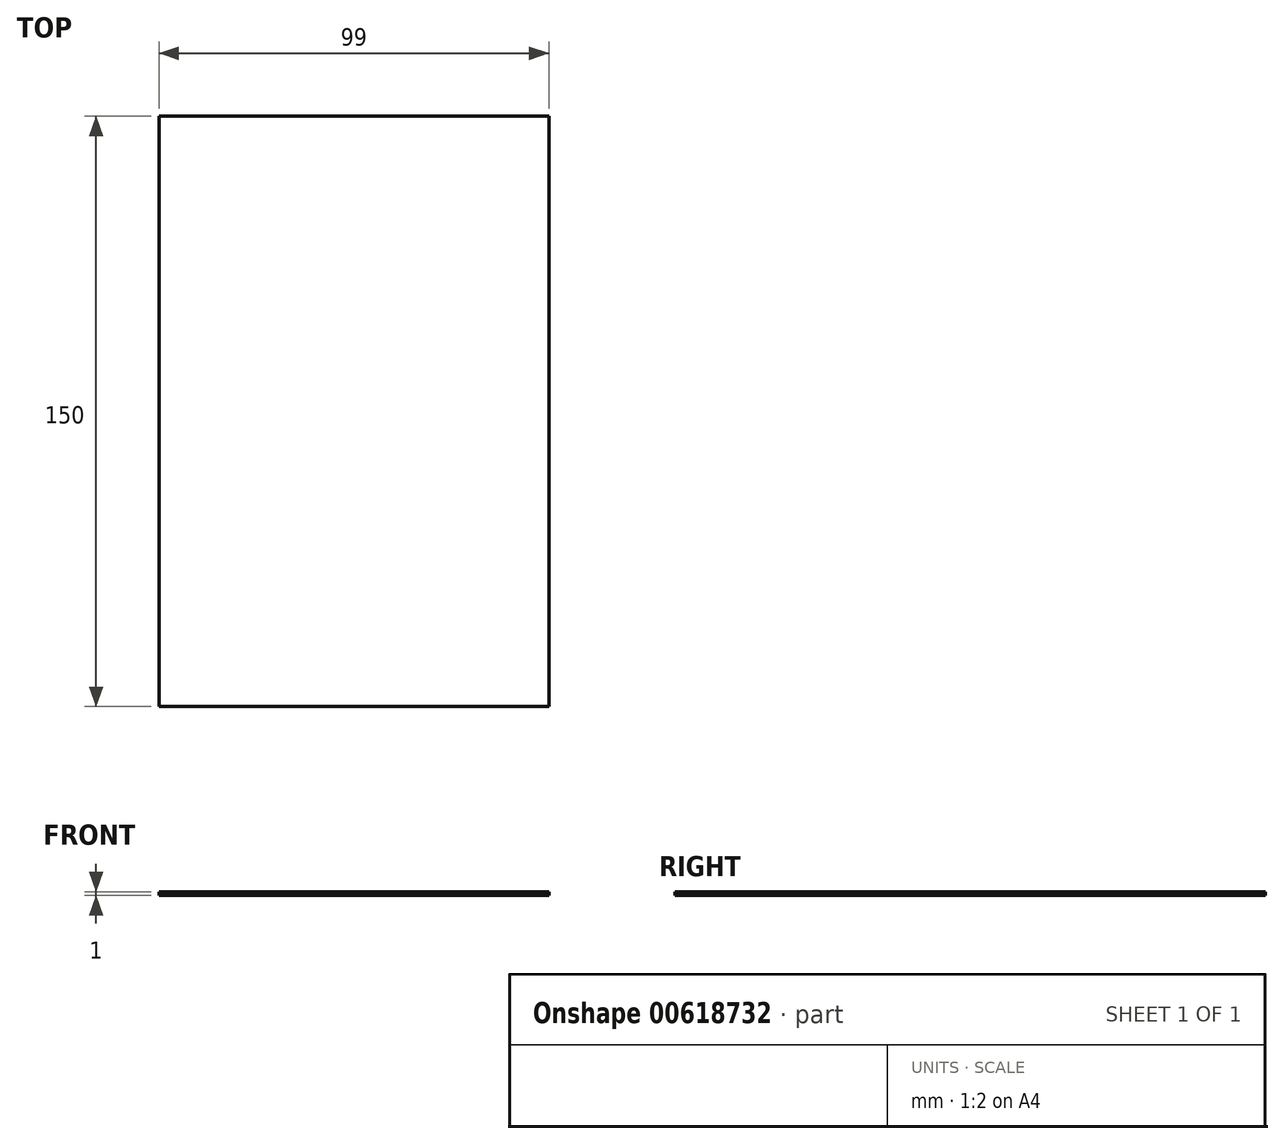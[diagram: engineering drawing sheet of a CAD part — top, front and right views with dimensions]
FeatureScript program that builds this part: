
annotation { "Feature Type Name" : "Feature", "Feature Type Description" : "" }
export const myFeature = defineFeature(function(context is Context, id is Id, definition is map)
    precondition{}
    {
        {
            var Q0;
            Q0=qCreatedBy(makeId("Top.planeOp"),FACE);
            var sketch = newSketch(context, id + "F0", { "sketchPlane" : qUnion([Q0])});
            skLineSegment(sketch, "E0.bottom", {"start": v(-46.67, 55.17) * mm, "end": v(52.33, 55.17) * mm});
            skLineSegment(sketch, "E0.top", {"start": v(-46.67, -94.83) * mm, "end": v(52.33, -94.83) * mm});
            skLineSegment(sketch, "E0.left", {"start": v(-46.67, 55.17) * mm, "end": v(-46.67, -94.83) * mm});
            skLineSegment(sketch, "E0.right", {"start": v(52.33, 55.17) * mm, "end": v(52.33, -94.83) * mm});
            skSolve(sketch);
        }
        {
            var Q0;
            Q0 = qSketchRegion(id + "F0", true);
            extrude(context, id + "F1", {"entities" : qUnion([Q0]), "depth" : 1 * mm, "offsetDistance" : 25 * mm});
        }
        {
            var Q0;
            Q0=qCreatedBy(makeId("Top.planeOp"),FACE);
            var sketch = newSketch(context, id + "F2", { "sketchPlane" : qUnion([Q0])});
            skLineSegment(sketch, "E1", {"start": v(-46.67, 38.54) * mm, "end": v(-38, 33.13) * mm});
            skLineSegment(sketch, "E2", {"start": v(-38, 33.13) * mm, "end": v(-46.67, 27.4) * mm});
            skLineSegment(sketch, "E3", {"start": v(-46.67, 27.4) * mm, "end": v(-38, 24.01) * mm});
            skLineSegment(sketch, "E4", {"start": v(-38, 24.01) * mm, "end": v(-46.67, 18.27) * mm});
            skLineSegment(sketch, "E5", {"start": v(-46.67, 18.27) * mm, "end": v(-38, 13.54) * mm});
            skLineSegment(sketch, "E6", {"start": v(-38, 13.54) * mm, "end": v(-46.67, 7.8) * mm});
            skLineSegment(sketch, "E7", {"start": v(-46.67, 7.8) * mm, "end": v(-38, 4.75) * mm});
            skLineSegment(sketch, "E8", {"start": v(-38, 4.75) * mm, "end": v(-45.17, 0) * mm});
            skLineSegment(sketch, "E9", {"start": v(-45.17, 0) * mm, "end": v(-69.1, 24.01) * mm});
            skLineSegment(sketch, "E10", {"start": v(-69.1, 24.01) * mm, "end": v(-46.67, 38.54) * mm});
            skSolve(sketch);
        }
        {
            var Q0;
            Q0 = qSketchRegion(id + "F2", true);
            extrude(context, id + "F3", {"entities" : qUnion([Q0]), "operationType" : NewBodyOperationType.REMOVE, "oppositeDirection" : true, "depth" : 25 * mm, "offsetDistance" : 25 * mm});
        }
    });
